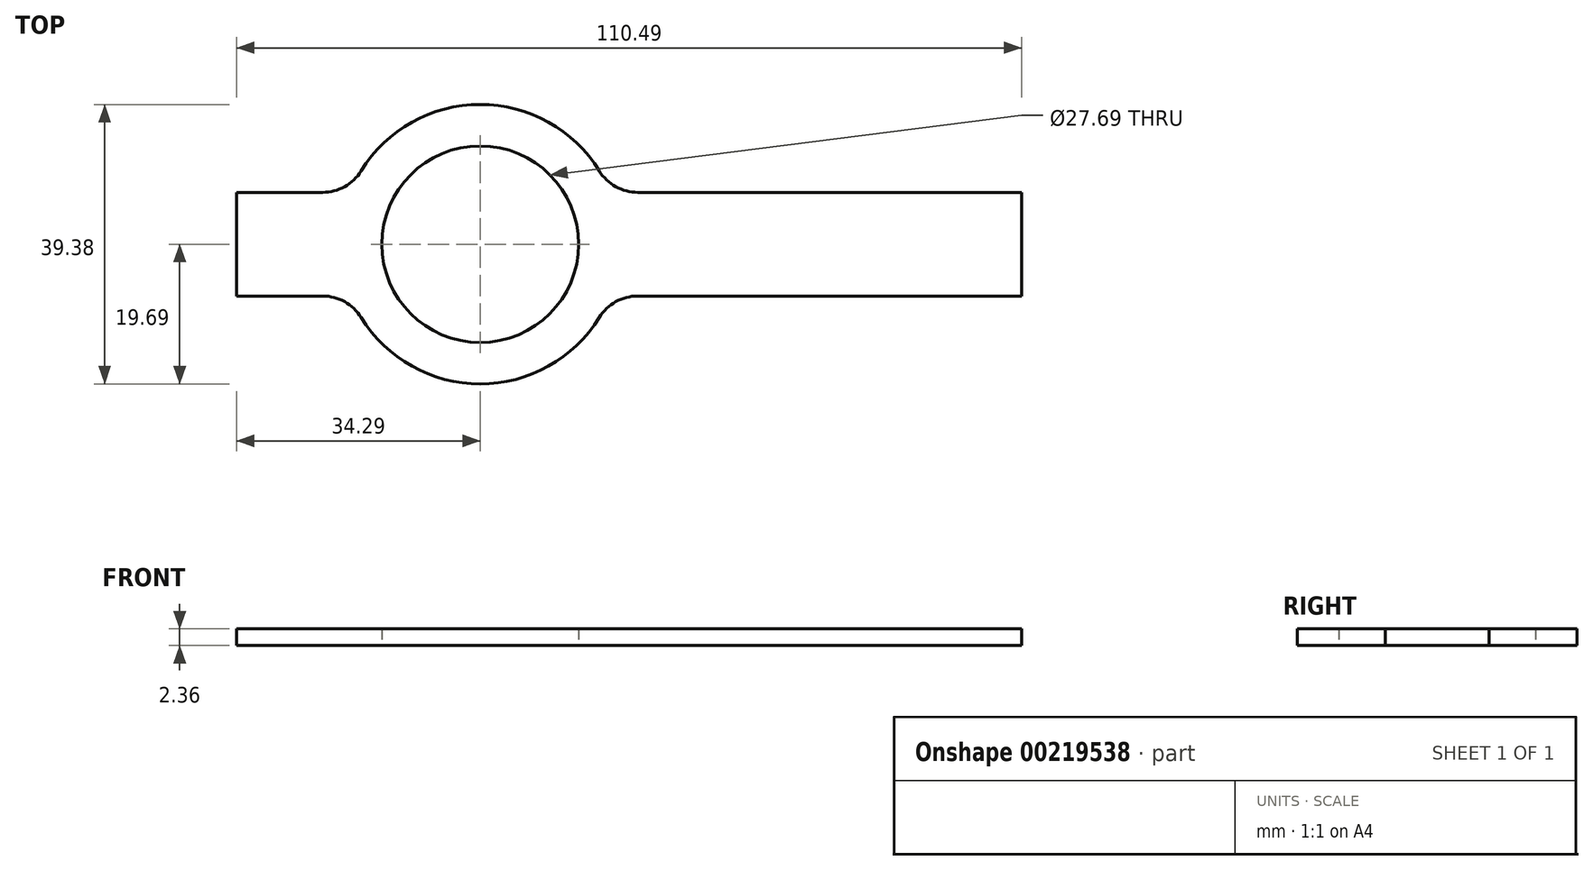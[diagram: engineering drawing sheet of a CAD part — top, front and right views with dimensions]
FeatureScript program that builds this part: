
annotation { "Feature Type Name" : "Feature", "Feature Type Description" : "" }
export const myFeature = defineFeature(function(context is Context, id is Id, definition is map)
    precondition{}
    {
        {
            var Q0;
            Q0=qCreatedBy(makeId("Top.planeOp"),FACE);
            var sketch = newSketch(context, id + "F0", { "sketchPlane" : qUnion([Q0])});
            skCircle(sketch, "E0", {"center": v(0, 0) * mm, "radius": 13.84 * mm});
            skCircle(sketch, "E1", {"center": v(0, 0) * mm, "radius": 19.69 * mm});
            skLineSegment(sketch, "E2", {"start": v(18.28, 7.3) * mm, "end": v(76.2, 7.3) * mm});
            skLineSegment(sketch, "E3", {"start": v(76.2, 7.3) * mm, "end": v(76.2, -7.3) * mm});
            skLineSegment(sketch, "E4", {"start": v(76.2, -7.3) * mm, "end": v(18.28, -7.3) * mm});
            skLineSegment(sketch, "E5", {"start": v(76.2, 0) * mm, "end": v(0, 0) * mm, "construction": true});
            skLineSegment(sketch, "E6", {"start": v(-18.28, 7.3) * mm, "end": v(-34.3, 7.3) * mm});
            skLineSegment(sketch, "E7", {"start": v(-34.3, 7.3) * mm, "end": v(-34.3, -7.3) * mm});
            skLineSegment(sketch, "E8", {"start": v(-34.3, -7.3) * mm, "end": v(-18.28, -7.3) * mm});
            skLineSegment(sketch, "E9", {"start": v(-34.3, 0) * mm, "end": v(0, 0) * mm, "construction": true});
            skSolve(sketch);
        }
        {
            var Q0;
            {var subQ0=sQuery(id+"F0.wireOp",EDGE,"E6");Q0=makeQuery(id+"F0.imprint","IMPRINT",FACE,{"disambiguationData":[TD([[makeQuery(id+"F0.imprint","IMPRINT",EDGE,{"derivedFrom":subQ0}),1.0]])]});}
            var Q1;
            Q1=makeQuery(id+"F0.imprint","IMPRINT",FACE,{"disambiguationData":[TD([[makeQuery(id+"F0.imprint","IMPRINT",EDGE,{"derivedFrom":sQuery(id+"F0.wireOp",EDGE,"E0")}),-1.0]])]});
            var Q2;
            {var subQ0=sQuery(id+"F0.wireOp",EDGE,"E2");Q2=makeQuery(id+"F0.imprint","IMPRINT",FACE,{"disambiguationData":[TD([[makeQuery(id+"F0.imprint","IMPRINT",EDGE,{"derivedFrom":subQ0}),-1.0]])]});}
            extrude(context, id + "F1", {"entities" : qUnion([Q0, Q1, Q2]), "depth" : 2.36 * mm});
        }
        {
            var Q0;
            Q0=makeQuery(id+"F1.opExtrude","SWEPT_EDGE",EDGE,{"disambiguationData":[OSD([sQuery(id+"F0.wireOp",EDGE,"E1"),sQuery(id+"F0.wireOp",EDGE,"E4")])]});
            var Q1;
            Q1=makeQuery(id+"F1.opExtrude","SWEPT_EDGE",EDGE,{"disambiguationData":[OSD([sQuery(id+"F0.wireOp",EDGE,"E1"),sQuery(id+"F0.wireOp",EDGE,"E8")])]});
            var Q2;
            Q2=makeQuery(id+"F1.opExtrude","SWEPT_EDGE",EDGE,{"disambiguationData":[OSD([sQuery(id+"F0.wireOp",EDGE,"E1"),sQuery(id+"F0.wireOp",EDGE,"E6")])]});
            var Q3;
            Q3=makeQuery(id+"F1.opExtrude","SWEPT_EDGE",EDGE,{"disambiguationData":[OSD([sQuery(id+"F0.wireOp",EDGE,"E1"),sQuery(id+"F0.wireOp",EDGE,"E2")])]});
            fillet(context, id + "F2", {"entities" : qUnion([Q0, Q1, Q2, Q3]), "radius" : 6.35 * mm, "tangentPropagation" : true, "allowEdgeOverflow" : false});
        }
    });
